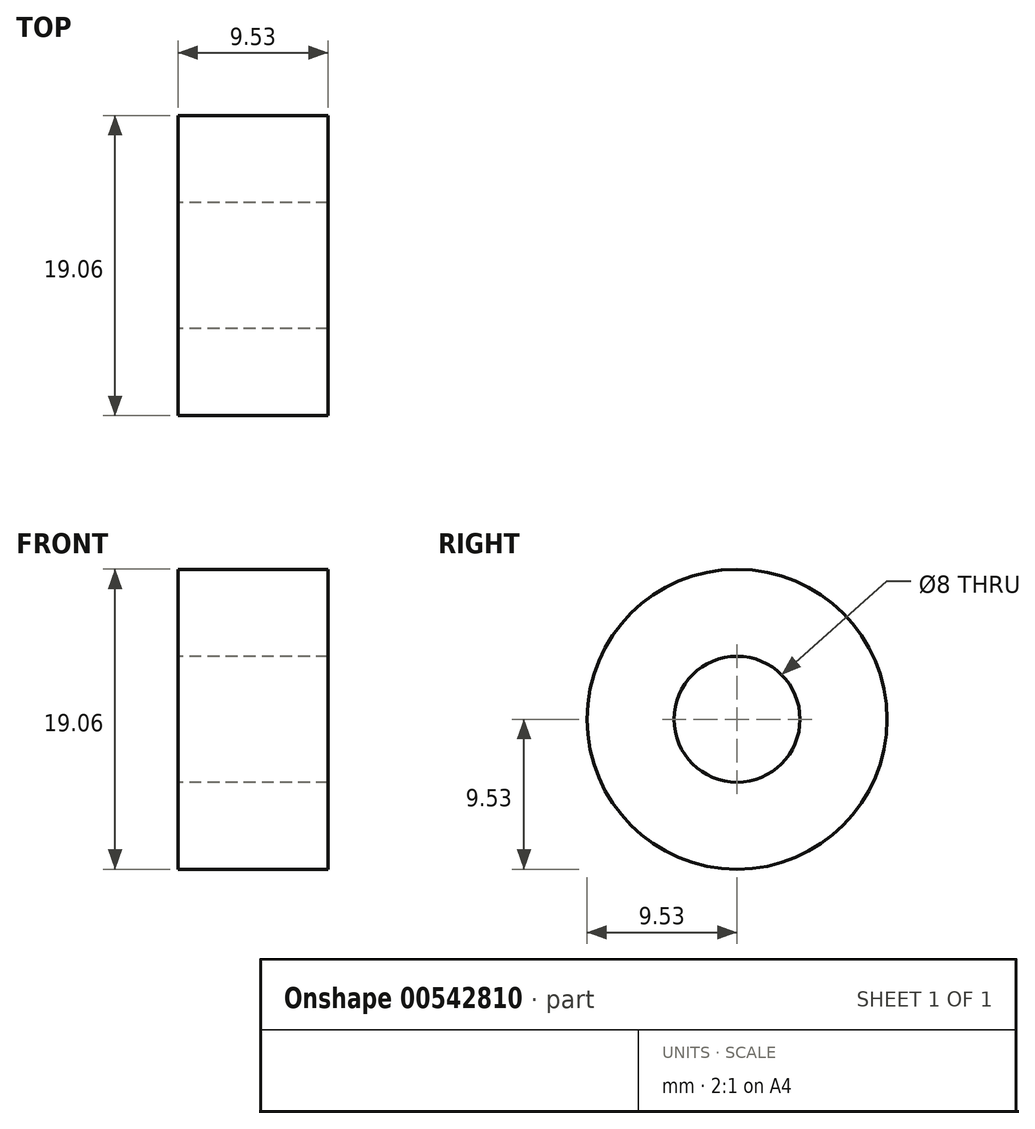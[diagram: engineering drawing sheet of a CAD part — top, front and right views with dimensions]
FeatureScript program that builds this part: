
annotation { "Feature Type Name" : "Feature", "Feature Type Description" : "" }
export const myFeature = defineFeature(function(context is Context, id is Id, definition is map)
    precondition{}
    {
        {
            var Q0;
            Q0=qCreatedBy(makeId("Right.planeOp"),FACE);
            var sketch = newSketch(context, id + "F0", { "sketchPlane" : qUnion([Q0])});
            skCircle(sketch, "E0", {"center": v(0, 0) * mm, "radius": 4 * mm});
            skCircle(sketch, "E1", {"center": v(0, 0) * mm, "radius": 9.53 * mm});
            skSolve(sketch);
        }
        {
            var Q0;
            Q0=qSketchRegion(id+"F0",true);
            extrude(context, id + "F1", {"entities" : qUnion([Q0]), "depth" : 9.52 * mm});
        }
    });
